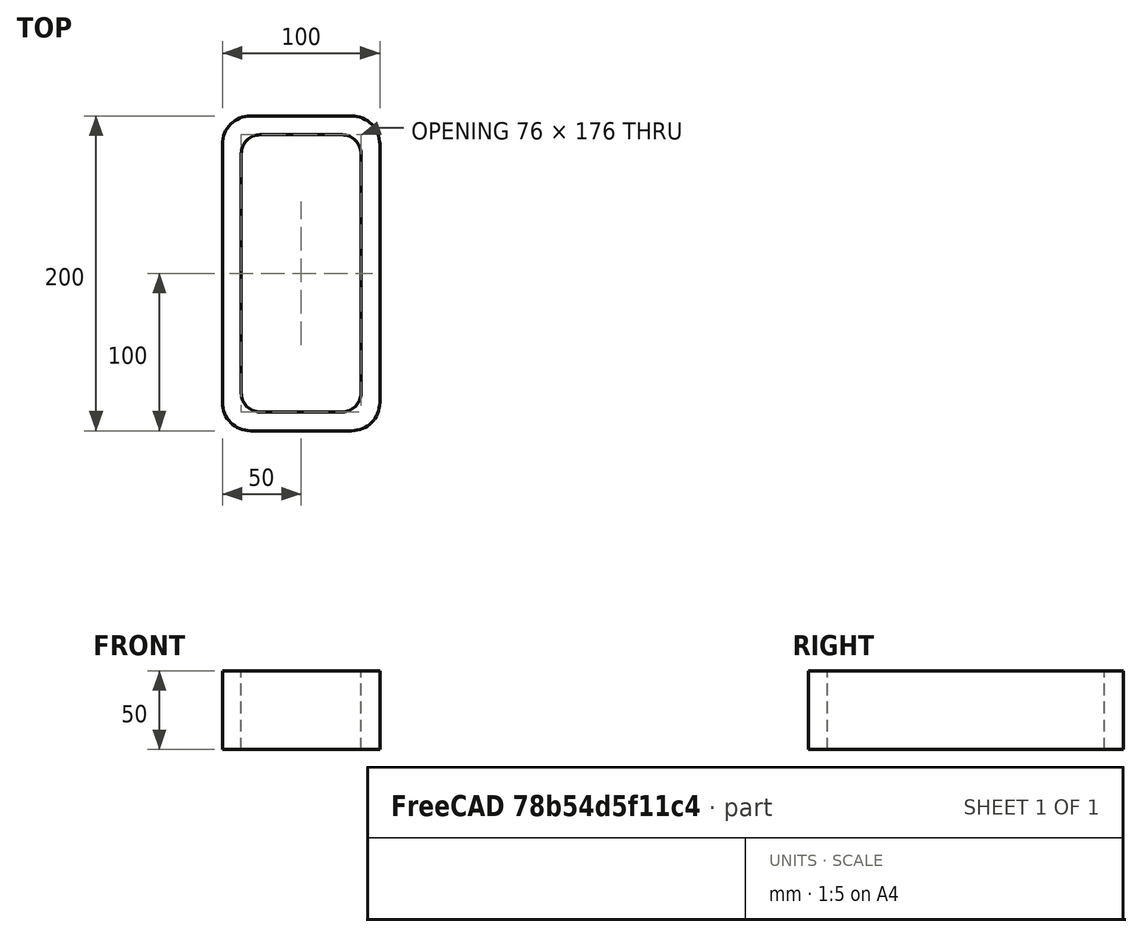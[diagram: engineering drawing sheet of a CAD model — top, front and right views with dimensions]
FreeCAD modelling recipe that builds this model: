
FCSTD DOCUMENT  (FreeCAD 0.15R4671 (Git))
Label: Rectangular hollow section 200x100x12 EN10219 S235JRH
License: All rights reserved
LicenseURL: http://en.wikipedia.org/wiki/All_rights_reserved
objects: Sketcher::SketchObject×1, Part::Extrusion×1
note: 2 computed .brp shape members not serialized (recipe doc carries the construction recipe); baked Part::Feature solids carry a one-line shape summary decoded from their .brp

FEATURE [Sketcher::SketchObject] Sketch
  sketch-geometry (16):
    g0: LineSegment StartX=-26 StartY=88 StartZ=0 EndX=26 EndY=88 EndZ=0
    g1: LineSegment StartX=38 StartY=76 StartZ=0 EndX=38 EndY=-76 EndZ=0
    g2: LineSegment StartX=26 StartY=-88 StartZ=0 EndX=-26 EndY=-88 EndZ=0
    g3: LineSegment StartX=-38 StartY=-76 StartZ=0 EndX=-38 EndY=76 EndZ=0
    g4: LineSegment StartX=-32 StartY=100 StartZ=0 EndX=32 EndY=100 EndZ=0
    g5: LineSegment StartX=50 StartY=82 StartZ=0 EndX=50 EndY=-82 EndZ=0
    g6: LineSegment StartX=32 StartY=-100 StartZ=0 EndX=-32 EndY=-100 EndZ=0
    g7: LineSegment StartX=-50 StartY=-82 StartZ=0 EndX=-50 EndY=82 EndZ=0
    g8: ArcOfCircle CenterX=-26 CenterY=76 CenterZ=0 NormalX=0 NormalY=0 NormalZ=1 Radius=12 StartAngle=1.5708 EndAngle=3.14159
    g9: ArcOfCircle CenterX=26 CenterY=76 CenterZ=0 NormalX=0 NormalY=0 NormalZ=1 Radius=12 StartAngle=0 EndAngle=1.5708
    g10: ArcOfCircle CenterX=26 CenterY=-76 CenterZ=0 NormalX=0 NormalY=0 NormalZ=1 Radius=12 StartAngle=4.71239 EndAngle=6.28319
    g11: ArcOfCircle CenterX=-26 CenterY=-76 CenterZ=0 NormalX=0 NormalY=0 NormalZ=1 Radius=12 StartAngle=3.14159 EndAngle=4.71239
    g12: ArcOfCircle CenterX=32 CenterY=82 CenterZ=0 NormalX=0 NormalY=0 NormalZ=1 Radius=18 StartAngle=0 EndAngle=1.5708
    g13: ArcOfCircle CenterX=32 CenterY=-82 CenterZ=0 NormalX=0 NormalY=0 NormalZ=1 Radius=18 StartAngle=4.71239 EndAngle=6.28319
    g14: ArcOfCircle CenterX=-32 CenterY=-82 CenterZ=0 NormalX=0 NormalY=0 NormalZ=1 Radius=18 StartAngle=3.14159 EndAngle=4.71239
    g15: ArcOfCircle CenterX=-32 CenterY=82 CenterZ=0 NormalX=0 NormalY=0 NormalZ=1 Radius=18 StartAngle=1.5708 EndAngle=3.14159
  constraints (36):
    c: Horizontal(g2)
    c: Vertical(g3)
    c: Horizontal(g6)
    c: Vertical(g7)
    c: Tangent(g3,g8) = 1.5708
    c: Tangent(g0,g8) = 1.5708
    c: Tangent(g0,g9) = 1.5708
    c: Tangent(g1,g9) = 1.5708
    c: Tangent(g1,g10) = 1.5708
    c: Tangent(g2,g10) = 1.5708
    c: Tangent(g2,g11) = 1.5708
    c: Tangent(g3,g11) = 1.5708
    c: Tangent(g4,g12) = 1.5708
    c: Tangent(g5,g12) = 1.5708
    c: Tangent(g5,g13) = 1.5708
    c: Tangent(g6,g13) = 1.5708
    c: Tangent(g6,g14) = 1.5708
    c: Tangent(g7,g14) = 1.5708
    c: Tangent(g7,g15) = 1.5708
    c: Tangent(g4,g15) = 1.5708
    c: Equal(g9,g8)
    c: Equal(g9,g11)
    c: Equal(g9,g10)
    c: Equal(g12,g15)
    c: Equal(g12,g14)
    c: Equal(g12,g13)
    c: Symmetric(g4,g6,g-1)
    c: Symmetric(g7,g5,g-2)
    c: DistanceY(g4,g6) = -200
    c: DistanceX(g7,g5) = 100
    c: Symmetric(g3,g1,g-2)
    c: Symmetric(g0,g2,g-1)
    c: DistanceY(g0,g4) = 12
    c: DistanceX(g5,g1) = -12
    c: Radius(g9) = 12
    c: Radius(g12) = 18
FEATURE [Part::Extrusion] Extrude  label="Rectangular hollow section 200x100x12 EN10219 S235JRH"
  Base = -> Sketch
  Dir = (0,0,50)
  Solid = true
